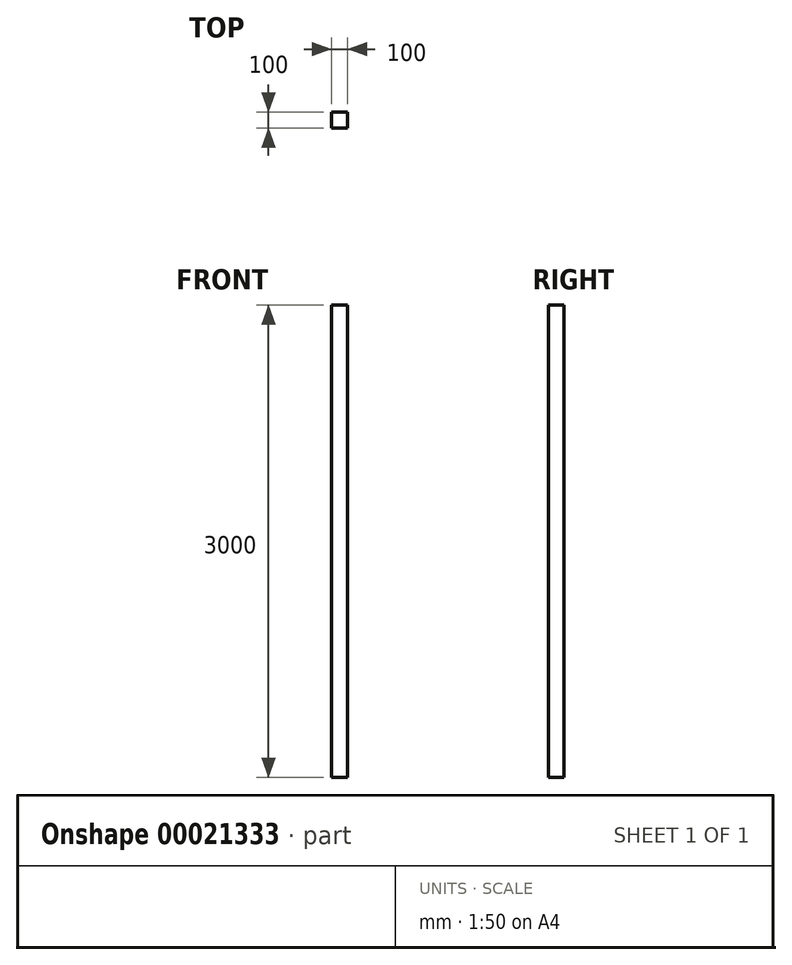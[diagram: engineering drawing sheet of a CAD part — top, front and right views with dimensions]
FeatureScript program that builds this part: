
annotation { "Feature Type Name" : "Feature", "Feature Type Description" : "" }
export const myFeature = defineFeature(function(context is Context, id is Id, definition is map)
    precondition{}
    {
        {
            var Q0;
            Q0=qCreatedBy(makeId("Top.planeOp"),FACE);
            var sketch = newSketch(context, id + "F0", { "sketchPlane" : qUnion([Q0])});
            skLineSegment(sketch, "E0.bottom", {"start": v(0, 0) * mm, "end": v(100, 0) * mm});
            skLineSegment(sketch, "E0.top", {"start": v(0, -100) * mm, "end": v(100, -100) * mm});
            skLineSegment(sketch, "E0.left", {"start": v(0, 0) * mm, "end": v(0, -100) * mm});
            skLineSegment(sketch, "E0.right", {"start": v(100, 0) * mm, "end": v(100, -100) * mm});
            skSolve(sketch);
        }
        {
            var Q0;
            Q0 = qSketchRegion(id + "F0", true);
            var Q1;
            Q1=makeQuery(id+"F0.imprint","IMPRINT",FACE,{"disambiguationData":[TD([[makeQuery(id+"F0.imprint","IMPRINT",EDGE,{"derivedFrom":sQuery(id+"F0.wireOp",EDGE,"E0.bottom")}),-1.0]])]});
            extrude(context, id + "F1", {"entities" : qUnion([Q0, Q1]), "depth" : 3000 * mm});
        }
    });
